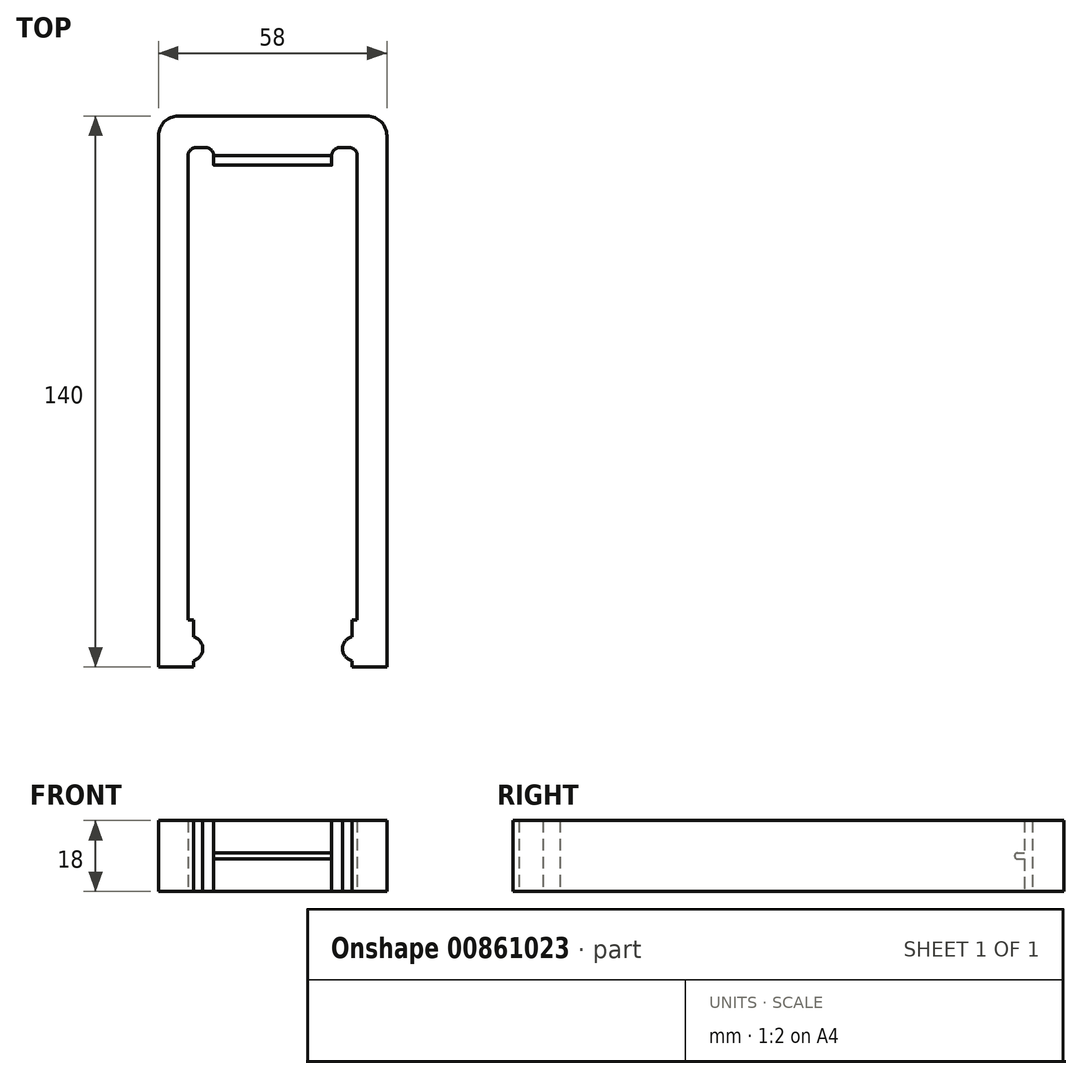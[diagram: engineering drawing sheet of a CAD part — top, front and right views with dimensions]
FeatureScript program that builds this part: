
annotation { "Feature Type Name" : "Feature", "Feature Type Description" : "" }
export const myFeature = defineFeature(function(context is Context, id is Id, definition is map)
    precondition{}
    {
        {
            assignVariable(context, id + "F0", {"name" : "NubWidth", "anyValue" : 1.5});
        }
        {
            var Q0;
            Q0=qCreatedBy(makeId("Top.planeOp"),FACE);
            var sketch = newSketch(context, id + "F1", { "sketchPlane" : qUnion([Q0])});
            skLineSegment(sketch, "E0", {"start": v(0, 0) * mm, "end": v(0, 140) * mm, "construction": true});
            skLineSegment(sketch, "E1", {"start": v(0, 140) * mm, "end": v(-24, 140) * mm});
            skLineSegment(sketch, "E2", {"start": v(-29, 0) * mm, "end": v(-20.15, 0) * mm});
            skLineSegment(sketch, "E3", {"start": v(-20.15, 0) * mm, "end": v(-20.15, 1.6) * mm});
            skLineSegment(sketch, "E4", {"start": v(-29, 135) * mm, "end": v(-29, 0) * mm});
            skLineSegment(sketch, "E5", {"start": v(-20.15, 7.7) * mm, "end": v(-20.15, 12) * mm});
            skLineSegment(sketch, "E6", {"start": v(-20.15, 12) * mm, "end": v(-21.5, 12) * mm});
            skLineSegment(sketch, "E7", {"start": v(-21.5, 12) * mm, "end": v(-21.5, 130) * mm});
            skCircle(sketch, "E8", {"center": v(-20.89, 4.65) * mm, "radius": 3.14 * mm, "construction": true});
            skPoint(sketch, "E8.third.point", {"position": v(-24.02, 4.57) * mm});
            skLineSegment(sketch, "E9", {"start": v(-20.15, 7.7) * mm, "end": v(-20.15, 1.6) * mm, "construction": true});
            skArc(sketch, "E10", {"start": v(-20.15, 7.7) * mm, "mid": v(-17.75, 4.65) * mm, "end": v(-20.15, 1.6) * mm});
            skPoint(sketch, "E11.visualSharp", {"position": v(-29, 140) * mm});
            skArc(sketch, "E11.filletArc", {"start": v(-24, 140) * mm, "mid": v(-27.54, 138.54) * mm, "end": v(-29, 135) * mm});
            skLineSegment(sketch, "E12", {"start": v(0, 130) * mm, "end": v(-15, 130) * mm});
            skLineSegment(sketch, "E13", {"start": v(-15, 130) * mm, "end": v(-15, 130) * mm});
            skLineSegment(sketch, "E14", {"start": v(-21.5, 130) * mm, "end": v(-21.5, 130) * mm});
            skLineSegment(sketch, "E15", {"start": v(-19.5, 132) * mm, "end": v(-17, 132) * mm});
            skPoint(sketch, "E16.visualSharp", {"position": v(-21.5, 132) * mm});
            skArc(sketch, "E16.filletArc", {"start": v(-19.5, 132) * mm, "mid": v(-20.91, 131.41) * mm, "end": v(-21.5, 130) * mm});
            skPoint(sketch, "E17.visualSharp", {"position": v(-15, 132) * mm});
            skArc(sketch, "E17.filletArc", {"start": v(-15, 130) * mm, "mid": v(-15.59, 131.41) * mm, "end": v(-17, 132) * mm});
            skLineSegment(sketch, "E18.MirrorCS", {"start": v(19.5, 132) * mm, "end": v(17, 132) * mm});
            skArc(sketch, "E19.MirrorCS", {"start": v(15, 130) * mm, "mid": v(15.59, 131.41) * mm, "end": v(17, 132) * mm});
            skArc(sketch, "E20.MirrorCS", {"start": v(19.5, 132) * mm, "mid": v(20.91, 131.41) * mm, "end": v(21.5, 130) * mm});
            skLineSegment(sketch, "E21.MirrorCS", {"start": v(20.15, 0) * mm, "end": v(20.15, 1.6) * mm});
            skLineSegment(sketch, "E22.MirrorCS", {"start": v(20.15, 12) * mm, "end": v(21.5, 12) * mm});
            skLineSegment(sketch, "E23.MirrorCS", {"start": v(20.15, 7.7) * mm, "end": v(20.15, 1.6) * mm, "construction": true});
            skLineSegment(sketch, "E24.MirrorCS", {"start": v(20.15, 7.7) * mm, "end": v(20.15, 12) * mm});
            skArc(sketch, "E25.MirrorCS", {"start": v(24, 140) * mm, "mid": v(27.54, 138.54) * mm, "end": v(29, 135) * mm});
            skArc(sketch, "E26.MirrorCS", {"start": v(20.15, 7.7) * mm, "mid": v(17.75, 4.65) * mm, "end": v(20.15, 1.6) * mm});
            skLineSegment(sketch, "E27.MirrorCS", {"start": v(0, 140) * mm, "end": v(24, 140) * mm});
            skLineSegment(sketch, "E28.MirrorCS", {"start": v(0, 130) * mm, "end": v(15, 130) * mm});
            skPoint(sketch, "E29.MirrorP", {"position": v(29, 140) * mm});
            skLineSegment(sketch, "E30.MirrorCS", {"start": v(29, 135) * mm, "end": v(29, 0) * mm});
            skLineSegment(sketch, "E31.MirrorCS", {"start": v(29, 0) * mm, "end": v(20.15, 0) * mm});
            skPoint(sketch, "E32.MirrorP", {"position": v(24.02, 4.57) * mm});
            skLineSegment(sketch, "E33.MirrorCS", {"start": v(15, 130) * mm, "end": v(15, 130) * mm});
            skLineSegment(sketch, "E34.MirrorCS", {"start": v(21.5, 12) * mm, "end": v(21.5, 130) * mm});
            skLineSegment(sketch, "E35.MirrorCS", {"start": v(21.5, 130) * mm, "end": v(21.5, 130) * mm});
            skPoint(sketch, "E36.MirrorP", {"position": v(21.5, 132) * mm});
            skPoint(sketch, "E37.MirrorP", {"position": v(15, 132) * mm});
            skCircle(sketch, "E38.MirrorC", {"center": v(20.89, 4.65) * mm, "radius": 3.14 * mm, "construction": true});
            skSolve(sketch);
        }
        {
            var Q0;
            Q0 = qSketchRegion(id + "F1", true);
            extrude(context, id + "F2", {"entities" : qUnion([Q0]), "depth" : 18 * mm, "offsetDistance" : 25 * mm});
        }
        {
            var Q0;
            Q0=makeQuery(id+"F2.opExtrude","SWEPT_FACE",FACE,{"disambiguationData":[OSD([sQuery(id+"F1.wireOp",EDGE,"E12"),sQuery(id+"F1.wireOp",EDGE,"E28.MirrorCS")])]});
            var sketch = newSketch(context, id + "F3", { "sketchPlane" : qUnion([Q0])});
            skLineSegment(sketch, "E39", {"start": v(-15, 9) * mm, "end": v(15, 9) * mm, "construction": true});
            skLineSegment(sketch, "E40.bottom", {"start": v(15, 9.75) * mm, "end": v(-15, 9.75) * mm});
            skLineSegment(sketch, "E40.top", {"start": v(15, 8.25) * mm, "end": v(-15, 8.25) * mm});
            skLineSegment(sketch, "E40.left", {"start": v(15, 9.75) * mm, "end": v(15, 8.25) * mm});
            skLineSegment(sketch, "E40.right", {"start": v(-15, 9.75) * mm, "end": v(-15, 8.25) * mm});
            skPoint(sketch, "E40.middle", {"position": v(0, 9) * mm});
            skSolve(sketch);
        }
        {
            var Q0;
            Q0 = qSketchRegion(id + "F3", true);
            extrude(context, id + "F4", {"entities" : qUnion([Q0]), "operationType" : NewBodyOperationType.ADD, "depth" : 2.5 * mm, "offsetDistance" : 25 * mm});
        }
        {
            var Q0;
            Q0=makeQuery(id+"F4.opExtrude","CAP_EDGE",EDGE,{"disambiguationData":[OSD([sQuery(id+"F3.wireOp",EDGE,"E40.bottom")])],"isStart":false});
            fillet(context, id + "F5", {"entities" : qUnion([Q0]), "radius" : (getVariable(context, 'NubWidth') / 2) * mm, "tangentPropagation" : true, "allowEdgeOverflow" : false});
        }
        {
            var Q0;
            Q0=makeQuery(id+"F4.opExtrude","CAP_EDGE",EDGE,{"disambiguationData":[OSD([sQuery(id+"F3.wireOp",EDGE,"E40.top")])],"isStart":false});
            fillet(context, id + "F6", {"entities" : qUnion([Q0]), "radius" : (getVariable(context, 'NubWidth') / 2) * mm, "tangentPropagation" : true, "allowEdgeOverflow" : false});
        }
    });
